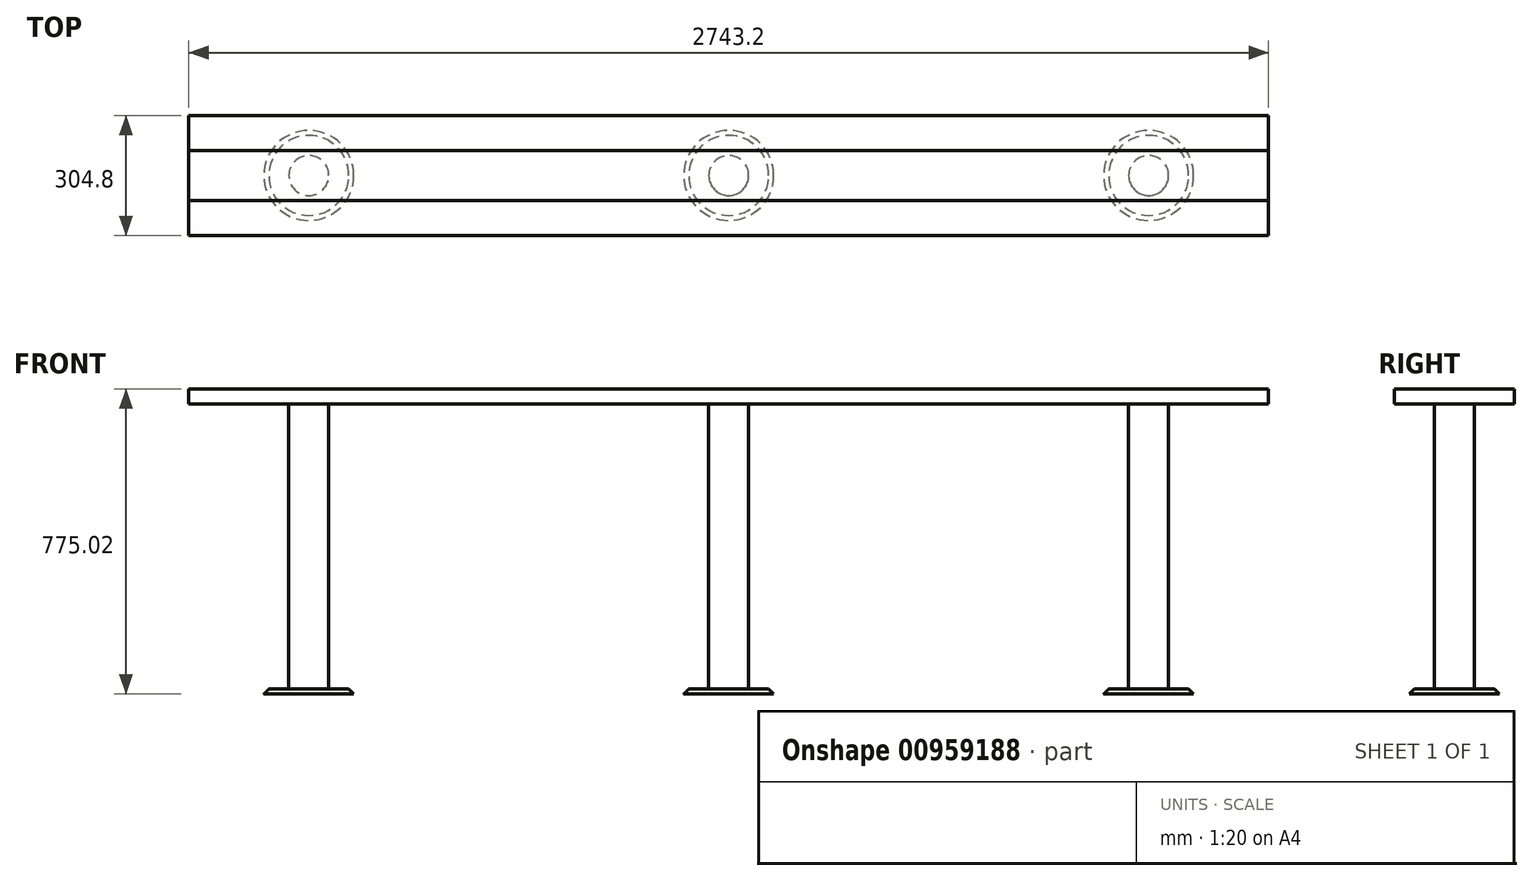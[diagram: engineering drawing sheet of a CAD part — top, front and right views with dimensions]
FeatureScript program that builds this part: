
annotation { "Feature Type Name" : "Feature", "Feature Type Description" : "" }
export const myFeature = defineFeature(function(context is Context, id is Id, definition is map)
    precondition{}
    {
        {
            var Q0;
            Q0=qCreatedBy(makeId("Top.planeOp"),FACE);
            var sketch = newSketch(context, id + "F0", { "sketchPlane" : qUnion([Q0])});
            skLineSegment(sketch, "E0.bottom", {"start": v(-1371.6, 152.4) * mm, "end": v(1371.6, 152.4) * mm});
            skLineSegment(sketch, "E0.top", {"start": v(-1371.6, -152.4) * mm, "end": v(1371.6, -152.4) * mm});
            skLineSegment(sketch, "E0.left", {"start": v(-1371.6, 152.4) * mm, "end": v(-1371.6, -152.4) * mm});
            skLineSegment(sketch, "E0.right", {"start": v(1371.6, 152.4) * mm, "end": v(1371.6, -152.4) * mm});
            skPoint(sketch, "E0.middle", {"position": v(0, 0) * mm});
            skLineSegment(sketch, "E1", {"start": v(-1582.85, 0) * mm, "end": v(1591.04, 0) * mm, "construction": true});
            skLineSegment(sketch, "E2", {"start": v(0, 320.12) * mm, "end": v(0, -316.17) * mm, "construction": true});
            skSolve(sketch);
        }
        {
            var Q0;
            Q0 = qSketchRegion(id + "F0", true);
            extrude(context, id + "F1", {"entities" : qUnion([Q0]), "depth" : 38.1 * mm, "offsetDistance" : 25.4 * mm});
        }
        {
            var Q0;
            Q0=makeQuery(id+"F1.opExtrude","CAP_FACE",FACE,{"disambiguationData":[OSD([sQuery(id+"F0.wireOp",EDGE,"E0.bottom"),sQuery(id+"F0.wireOp",EDGE,"E0.top"),sQuery(id+"F0.wireOp",EDGE,"E0.left"),sQuery(id+"F0.wireOp",EDGE,"E0.right")])],"isStart":true});
            var sketch = newSketch(context, id + "F2", { "sketchPlane" : qUnion([Q0])});
            skLineSegment(sketch, "E3.0", {"start": v(-1582.85, 0) * mm, "end": v(1591.04, 0) * mm, "construction": true});
            skLineSegment(sketch, "E4.0", {"start": v(0, -320.12) * mm, "end": v(0, 316.17) * mm, "construction": true});
            skCircle(sketch, "E5", {"center": v(-1066.8, 0) * mm, "radius": 50.8 * mm});
            skCircle(sketch, "E6.MirrorC", {"center": v(1066.8, 0) * mm, "radius": 50.8 * mm});
            skCircle(sketch, "E7", {"center": v(0, 0) * mm, "radius": 50.8 * mm});
            skSolve(sketch);
        }
        {
            var Q0;
            Q0 = qSketchRegion(id + "F2", true);
            extrude(context, id + "F3", {"entities" : qUnion([Q0]), "operationType" : NewBodyOperationType.ADD, "depth" : 736.6 * mm, "offsetDistance" : 25.4 * mm});
        }
        {
            var Q0;
            Q0=makeQuery(id+"F3.opExtrude","CAP_FACE",FACE,{"disambiguationData":[OSD([sQuery(id+"F2.wireOp",EDGE,"E5")])],"isStart":false});
            var sketch = newSketch(context, id + "F4", { "sketchPlane" : qUnion([Q0])});
            skCircle(sketch, "E8", {"center": v(-1066.8, 0) * mm, "radius": 114.3 * mm});
            skCircle(sketch, "E9.MirrorC", {"center": v(1066.8, 0) * mm, "radius": 114.3 * mm});
            skCircle(sketch, "E10", {"center": v(0, 0) * mm, "radius": 114.3 * mm});
            skSolve(sketch);
        }
        {
            var Q0;
            Q0 = qSketchRegion(id + "F4", true);
            extrude(context, id + "F5", {"entities" : qUnion([Q0]), "operationType" : NewBodyOperationType.ADD, "oppositeDirection" : true, "depth" : 12.7 * mm, "offsetDistance" : 25.4 * mm, "hasDraft" : true, "draftAngle" : 45 * degree, "draftPullDirection" : true});
        }
        {
            var Q0;
            Q0=makeQuery(id+"F1.opExtrude","CAP_FACE",FACE,{"disambiguationData":[OSD([sQuery(id+"F0.wireOp",EDGE,"E0.bottom"),sQuery(id+"F0.wireOp",EDGE,"E0.top"),sQuery(id+"F0.wireOp",EDGE,"E0.left"),sQuery(id+"F0.wireOp",EDGE,"E0.right")])],"isStart":false});
            var sketch = newSketch(context, id + "F6", { "sketchPlane" : qUnion([Q0])});
            skLineSegment(sketch, "E11.0", {"start": v(-1371.6, 152.4) * mm, "end": v(1371.6, 152.4) * mm});
            skLineSegment(sketch, "E12.0", {"start": v(-1371.6, 152.4) * mm, "end": v(-1371.6, -152.4) * mm});
            skLineSegment(sketch, "E13.0", {"start": v(-1371.6, -152.4) * mm, "end": v(1371.6, -152.4) * mm});
            skLineSegment(sketch, "E14.0", {"start": v(1371.6, 152.4) * mm, "end": v(1371.6, -152.4) * mm});
            skLineSegment(sketch, "E15", {"start": v(-1371.6, 63.5) * mm, "end": v(1371.6, 63.5) * mm});
            skLineSegment(sketch, "E16", {"start": v(-1371.6, -63.5) * mm, "end": v(1371.6, -63.5) * mm});
            skSolve(sketch);
        }
        {
            var Q0;
            {var subQ0=sQuery(id+"F6.wireOp",EDGE,"E11.0");Q0=makeQuery(id+"F6.imprint","IMPRINT",FACE,{"disambiguationData":[TD([[makeQuery(id+"F6.imprint","IMPRINT",EDGE,{"derivedFrom":subQ0}),-1.0]])]});}
            var Q1;
            {var subQ0=sQuery(id+"F6.wireOp",EDGE,"E13.0");Q1=makeQuery(id+"F6.imprint","IMPRINT",FACE,{"disambiguationData":[TD([[makeQuery(id+"F6.imprint","IMPRINT",EDGE,{"derivedFrom":subQ0}),1.0]])]});}
            extrude(context, id + "F7", {"entities" : qUnion([Q0, Q1]), "operationType" : NewBodyOperationType.ADD, "depth" : 0.32 * mm, "offsetDistance" : 25.4 * mm});
        }
    });
